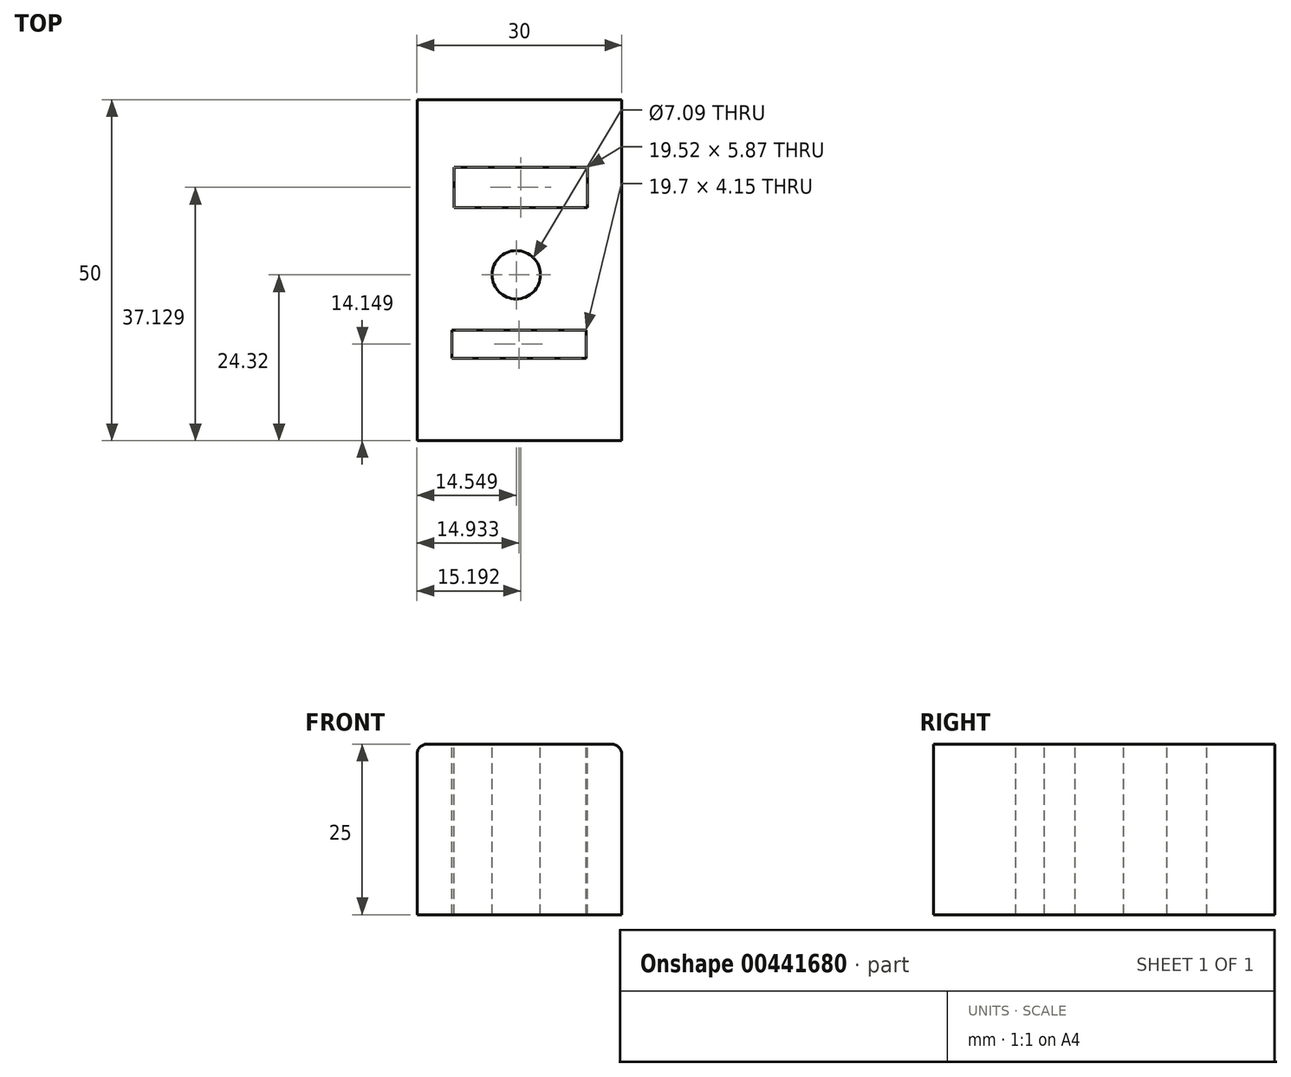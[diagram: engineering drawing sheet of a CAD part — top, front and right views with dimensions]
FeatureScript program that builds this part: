
annotation { "Feature Type Name" : "Feature", "Feature Type Description" : "" }
export const myFeature = defineFeature(function(context is Context, id is Id, definition is map)
    precondition{}
    {
        {
            var Q0;
            Q0=qCreatedBy(makeId("Top.planeOp"),FACE);
            var sketch = newSketch(context, id + "F0", { "sketchPlane" : qUnion([Q0])});
            skLineSegment(sketch, "E0.bottom", {"start": v(25.1, 25.68) * mm, "end": v(55.1, 25.68) * mm});
            skLineSegment(sketch, "E0.top", {"start": v(25.1, -24.32) * mm, "end": v(55.1, -24.32) * mm});
            skLineSegment(sketch, "E0.left", {"start": v(25.1, 25.68) * mm, "end": v(25.1, -24.32) * mm});
            skLineSegment(sketch, "E0.right", {"start": v(55.1, 25.68) * mm, "end": v(55.1, -24.32) * mm});
            skSolve(sketch);
        }
        {
            var Q0;
            Q0=makeQuery(id+"F0.imprint","IMPRINT",FACE,{"disambiguationData":[TD([[makeQuery(id+"F0.imprint","IMPRINT",EDGE,{"derivedFrom":sQuery(id+"F0.wireOp",EDGE,"E0.bottom")}),-1.0]])]});
            extrude(context, id + "F1", {"entities" : qUnion([Q0]), "depth" : 25 * mm});
        }
        {
            var Q0;
            Q0=makeQuery(id+"F1.opExtrude","CAP_FACE",FACE,{"disambiguationData":[OSD([sQuery(id+"F0.wireOp",EDGE,"E0.bottom"),sQuery(id+"F0.wireOp",EDGE,"E0.top"),sQuery(id+"F0.wireOp",EDGE,"E0.left"),sQuery(id+"F0.wireOp",EDGE,"E0.right")])],"isStart":false});
            var sketch = newSketch(context, id + "F2", { "sketchPlane" : qUnion([Q0])});
            skLineSegment(sketch, "E1.bottom", {"start": v(30.53, 15.75) * mm, "end": v(50.05, 15.75) * mm});
            skLineSegment(sketch, "E1.top", {"start": v(30.53, 9.87) * mm, "end": v(50.05, 9.87) * mm});
            skLineSegment(sketch, "E1.left", {"start": v(30.53, 15.75) * mm, "end": v(30.53, 9.87) * mm});
            skLineSegment(sketch, "E1.right", {"start": v(50.05, 15.75) * mm, "end": v(50.05, 9.87) * mm});
            skLineSegment(sketch, "E2.bottom", {"start": v(30.18, -8.1) * mm, "end": v(49.88, -8.1) * mm});
            skLineSegment(sketch, "E2.top", {"start": v(30.18, -12.25) * mm, "end": v(49.88, -12.25) * mm});
            skLineSegment(sketch, "E2.left", {"start": v(30.18, -8.1) * mm, "end": v(30.18, -12.25) * mm});
            skLineSegment(sketch, "E2.right", {"start": v(49.88, -8.1) * mm, "end": v(49.88, -12.25) * mm});
            skCircle(sketch, "E3", {"center": v(39.65, 0) * mm, "radius": 3.54 * mm});
            skSolve(sketch);
        }
        {
            var Q0;
            Q0=makeQuery(id+"F2.imprint","IMPRINT",FACE,{"disambiguationData":[TD([[makeQuery(id+"F2.imprint","IMPRINT",EDGE,{"derivedFrom":sQuery(id+"F2.wireOp",EDGE,"E2.bottom")}),-1.0]])]});
            var Q1;
            Q1=makeQuery(id+"F2.imprint","IMPRINT",FACE,{"disambiguationData":[TD([[makeQuery(id+"F2.imprint","IMPRINT",EDGE,{"derivedFrom":sQuery(id+"F2.wireOp",EDGE,"E1.bottom")}),-1.0]])]});
            extrude(context, id + "F3", {"entities" : qUnion([Q0, Q1]), "operationType" : NewBodyOperationType.ADD, "oppositeDirection" : true, "depth" : 10 * mm});
        }
        {
            var Q0;
            Q0=makeQuery(id+"F2.imprint","IMPRINT",FACE,{"disambiguationData":[TD([[makeQuery(id+"F2.imprint","IMPRINT",EDGE,{"derivedFrom":sQuery(id+"F2.wireOp",EDGE,"E1.bottom")}),-1.0]])]});
            var Q1;
            Q1=makeQuery(id+"F2.imprint","IMPRINT",FACE,{"disambiguationData":[TD([[makeQuery(id+"F2.imprint","IMPRINT",EDGE,{"derivedFrom":sQuery(id+"F2.wireOp",EDGE,"E2.bottom")}),-1.0]])]});
            extrude(context, id + "F4", {"entities" : qUnion([Q0, Q1]), "operationType" : NewBodyOperationType.ADD, "oppositeDirection" : true, "depth" : 10 * mm});
        }
        {
            var Q0;
            Q0=makeQuery(id+"F2.imprint","IMPRINT",FACE,{"disambiguationData":[TD([[makeQuery(id+"F2.imprint","IMPRINT",EDGE,{"derivedFrom":sQuery(id+"F2.wireOp",EDGE,"E1.bottom")}),-1.0]])]});
            extrude(context, id + "F5", {"entities" : qUnion([Q0]), "operationType" : NewBodyOperationType.REMOVE, "oppositeDirection" : true, "depth" : 25 * mm});
        }
        {
            var Q0;
            Q0=makeQuery(id+"F2.imprint","IMPRINT",FACE,{"disambiguationData":[TD([[makeQuery(id+"F2.imprint","IMPRINT",EDGE,{"derivedFrom":sQuery(id+"F2.wireOp",EDGE,"E2.bottom")}),-1.0]])]});
            extrude(context, id + "F6", {"entities" : qUnion([Q0]), "operationType" : NewBodyOperationType.REMOVE, "oppositeDirection" : true, "depth" : 25 * mm});
        }
        {
            var Q0;
            Q0=makeQuery(id+"F1.opExtrude","CAP_EDGE",EDGE,{"disambiguationData":[OSD([sQuery(id+"F0.wireOp",EDGE,"E0.right")])],"isStart":false});
            var Q1;
            Q1=makeQuery(id+"F1.opExtrude","CAP_EDGE",EDGE,{"disambiguationData":[OSD([sQuery(id+"F0.wireOp",EDGE,"E0.left")])],"isStart":false});
            fillet(context, id + "F7", {"entities" : qUnion([Q0, Q1]), "radius" : 1.5 * mm, "tangentPropagation" : true, "allowEdgeOverflow" : false});
        }
        {
            var Q0;
            Q0=makeQuery(id+"F2.imprint","IMPRINT",FACE,{"disambiguationData":[TD([[makeQuery(id+"F2.imprint","IMPRINT",EDGE,{"derivedFrom":sQuery(id+"F2.wireOp",EDGE,"E3")}),1.0]])]});
            extrude(context, id + "F8", {"entities" : qUnion([Q0]), "operationType" : NewBodyOperationType.REMOVE, "oppositeDirection" : true, "depth" : 25 * mm});
        }
    });
